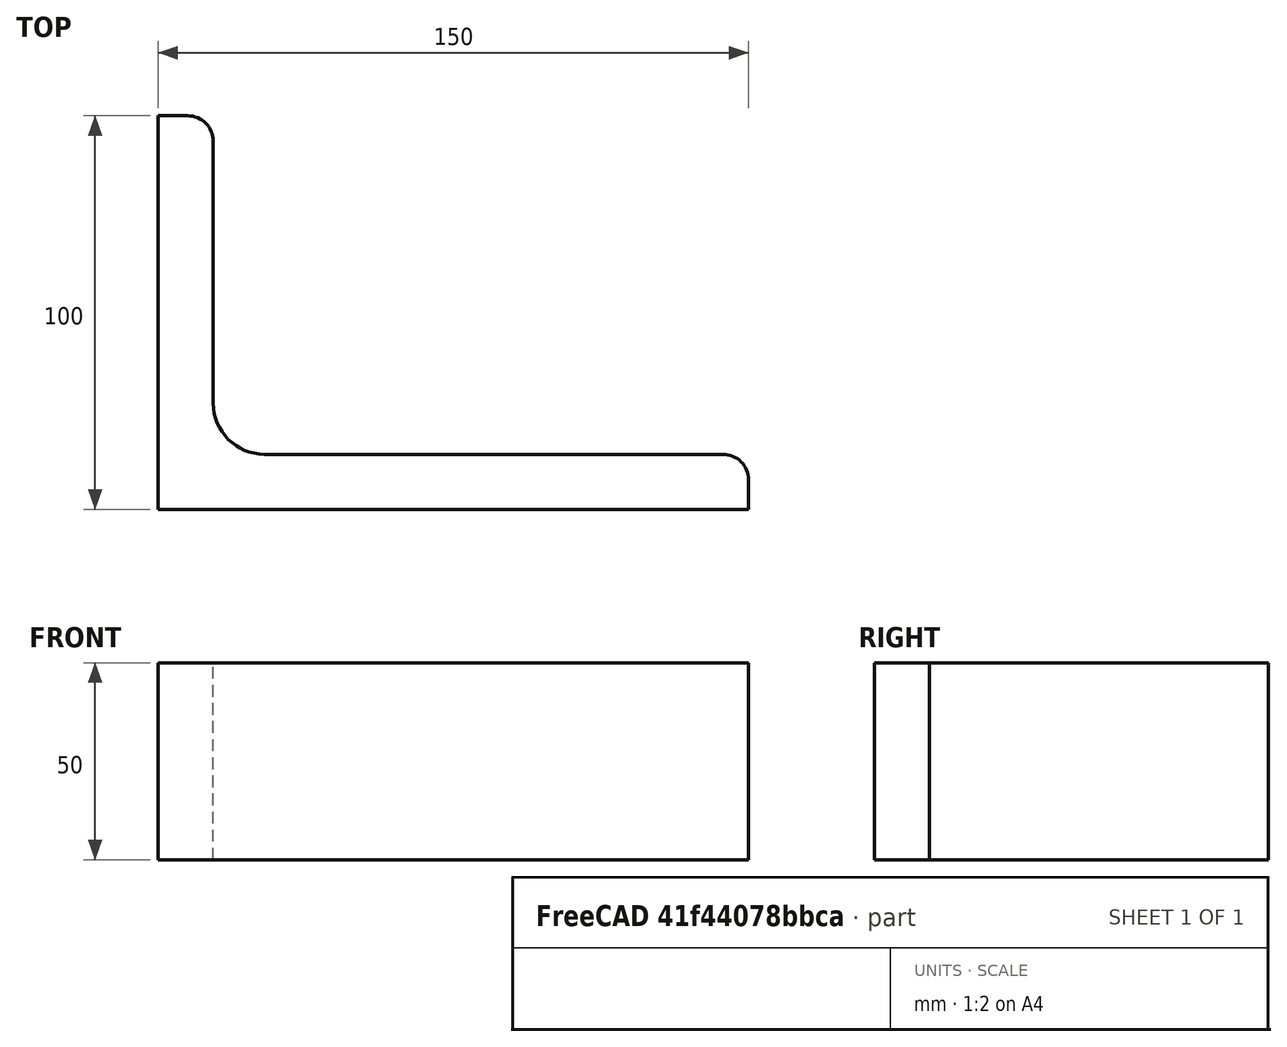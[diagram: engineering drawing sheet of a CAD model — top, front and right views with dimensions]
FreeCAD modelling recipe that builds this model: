
FCSTD DOCUMENT  (FreeCAD 0.15R4671 (Git))
Label: Angle Bar 150x100x14 EN10056 S235JR
License: All rights reserved
LicenseURL: http://en.wikipedia.org/wiki/All_rights_reserved
objects: Sketcher::SketchObject×1, Part::Extrusion×1
note: 2 computed .brp shape members not serialized (recipe doc carries the construction recipe); baked Part::Feature solids carry a one-line shape summary decoded from their .brp

FEATURE [Sketcher::SketchObject] Sketch
  sketch-geometry (9):
    g0: LineSegment StartX=0 StartY=0 StartZ=0 EndX=150 EndY=0 EndZ=0
    g1: LineSegment StartX=150 StartY=0 StartZ=0 EndX=150 EndY=7.5 EndZ=0
    g2: LineSegment StartX=143.5 StartY=14 StartZ=0 EndX=27 EndY=14 EndZ=0
    g3: LineSegment StartX=0 StartY=0 StartZ=0 EndX=0 EndY=100 EndZ=0
    g4: LineSegment StartX=0 StartY=100 StartZ=0 EndX=7.5 EndY=100 EndZ=0
    g5: LineSegment StartX=14 StartY=93.5 StartZ=0 EndX=14 EndY=27 EndZ=0
    g6: ArcOfCircle CenterX=27 CenterY=27 CenterZ=0 NormalX=0 NormalY=0 NormalZ=1 Radius=13 StartAngle=3.14159 EndAngle=4.71239
    g7: ArcOfCircle CenterX=7.5 CenterY=93.5 CenterZ=0 NormalX=0 NormalY=0 NormalZ=1 Radius=6.5 StartAngle=0 EndAngle=1.5708
    g8: ArcOfCircle CenterX=143.5 CenterY=7.5 CenterZ=0 NormalX=0 NormalY=0 NormalZ=1 Radius=6.5 StartAngle=0 EndAngle=1.5708
  constraints (23):
    c: Coincident(g0,g-1)
    c: Horizontal(g0)
    c: Coincident(g1,g0)
    c: Vertical(g1)
    c: Horizontal(g2)
    c: Coincident(g3,g-1)
    c: Vertical(g3)
    c: Coincident(g4,g3)
    c: Horizontal(g4)
    c: Vertical(g5)
    c: Tangent(g5,g6) = -1.5708
    c: Tangent(g2,g6) = 1.5708
    c: Tangent(g4,g7) = 1.5708
    c: Tangent(g5,g7) = 1.5708
    c: Tangent(g2,g8) = -1.5708
    c: Tangent(g1,g8) = -1.5708
    c: DistanceX(g0) = 150
    c: DistanceY(g3) = 100
    c: DistanceY(g0,g2) = 14
    c: DistanceX(g3,g5) = 14
    c: Radius(g6) = 13
    c: Radius(g8) = 6.5
    c: Radius(g7) = 6.5
FEATURE [Part::Extrusion] Extrude  label="Angle Bar 150x100x14 EN10056 S235JR"
  Base = -> Sketch
  Dir = (0,0,50)
  Solid = true
